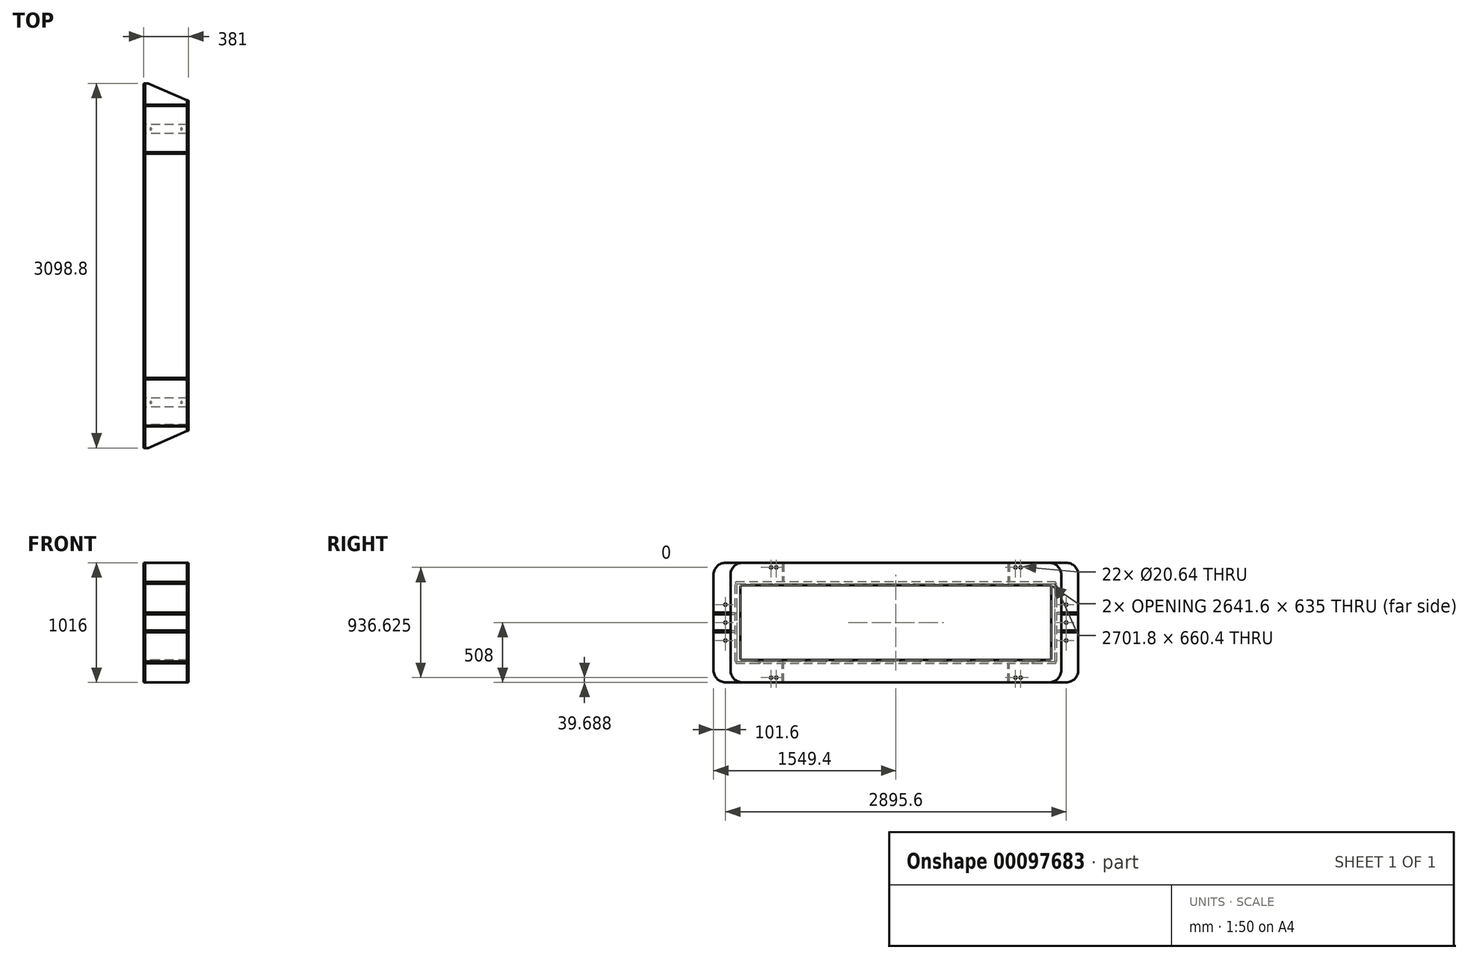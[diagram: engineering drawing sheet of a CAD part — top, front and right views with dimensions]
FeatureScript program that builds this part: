
annotation { "Feature Type Name" : "Feature", "Feature Type Description" : "" }
export const myFeature = defineFeature(function(context is Context, id is Id, definition is map)
    precondition{}
    {
        {
            var Q0;
            Q0=qCreatedBy(makeId("Right.planeOp"),FACE);
            var sketch = newSketch(context, id + "F0", { "sketchPlane" : qUnion([Q0])});
            skLineSegment(sketch, "E0.bottom", {"start": v(-1308.1, 317.5) * mm, "end": v(1308.1, 317.5) * mm});
            skLineSegment(sketch, "E0.top", {"start": v(-1308.1, -317.5) * mm, "end": v(1308.1, -317.5) * mm});
            skLineSegment(sketch, "E0.left", {"start": v(-1320.8, 304.8) * mm, "end": v(-1320.8, -304.8) * mm});
            skLineSegment(sketch, "E0.right", {"start": v(1320.8, 304.8) * mm, "end": v(1320.8, -304.8) * mm});
            skPoint(sketch, "E0.middle", {"position": v(0, 0) * mm});
            skLineSegment(sketch, "E1.bottom", {"start": v(-1447.8, 508) * mm, "end": v(1447.8, 508) * mm});
            skLineSegment(sketch, "E1.top", {"start": v(-1447.8, -508) * mm, "end": v(1447.8, -508) * mm});
            skLineSegment(sketch, "E1.left", {"start": v(-1549.4, 406.4) * mm, "end": v(-1549.4, -406.4) * mm});
            skLineSegment(sketch, "E1.right", {"start": v(1549.4, 406.4) * mm, "end": v(1549.4, -406.4) * mm});
            skLineSegment(sketch, "E2", {"start": v(-1633.4, 0) * mm, "end": v(1813.82, 0) * mm, "construction": true});
            skPoint(sketch, "E2.endSnap0", {"position": v(-1549.4, 0) * mm});
            skLineSegment(sketch, "E3", {"start": v(0, 873) * mm, "end": v(0, -1070.76) * mm, "construction": true});
            skLineSegment(sketch, "E4.0", {"start": v(-1447.8, 873) * mm, "end": v(-1447.8, -1070.76) * mm, "construction": true});
            skLineSegment(sketch, "E5.0", {"start": v(-1633.4, 152.4) * mm, "end": v(1813.82, 152.4) * mm, "construction": true});
            skLineSegment(sketch, "E6.0", {"start": v(-1633.4, -152.4) * mm, "end": v(1813.82, -152.4) * mm, "construction": true});
            skCircle(sketch, "E7", {"center": v(-1447.8, 152.4) * mm, "radius": 10.32 * mm});
            skCircle(sketch, "E8.0.1.0", {"center": v(-1447.8, 0) * mm, "radius": 10.32 * mm});
            skCircle(sketch, "E8.0.2.0", {"center": v(-1447.8, -152.4) * mm, "radius": 10.32 * mm});
            skLineSegment(sketch, "E8.direction1", {"start": v(-1447.8, 152.4) * mm, "end": v(-1422.4, 152.4) * mm, "construction": true});
            skLineSegment(sketch, "E8.direction2", {"start": v(-1447.8, 152.4) * mm, "end": v(-1447.8, 0) * mm, "construction": true});
            skLineSegment(sketch, "E9.MirrorCS", {"start": v(1447.8, 152.4) * mm, "end": v(1422.4, 152.4) * mm, "construction": true});
            skCircle(sketch, "E10.MirrorC", {"center": v(1447.8, 152.4) * mm, "radius": 10.32 * mm});
            skCircle(sketch, "E11.MirrorC", {"center": v(1447.8, 0) * mm, "radius": 10.32 * mm});
            skCircle(sketch, "E12.MirrorC", {"center": v(1447.8, -152.4) * mm, "radius": 10.32 * mm});
            skPoint(sketch, "E13.MirrorP", {"position": v(1549.4, 0) * mm});
            skLineSegment(sketch, "E14.MirrorCS", {"start": v(1447.8, 152.4) * mm, "end": v(1447.8, 0) * mm, "construction": true});
            skPoint(sketch, "E15.visualSharp", {"position": v(-1320.8, 317.5) * mm});
            skArc(sketch, "E15.filletArc", {"start": v(-1308.1, 317.5) * mm, "mid": v(-1317.08, 313.78) * mm, "end": v(-1320.8, 304.8) * mm});
            skPoint(sketch, "E16.visualSharp", {"position": v(-1320.8, -317.5) * mm});
            skArc(sketch, "E16.filletArc", {"start": v(-1320.8, -304.8) * mm, "mid": v(-1317.08, -313.78) * mm, "end": v(-1308.1, -317.5) * mm});
            skPoint(sketch, "E17.visualSharp", {"position": v(1320.8, -317.5) * mm});
            skArc(sketch, "E17.filletArc", {"start": v(1308.1, -317.5) * mm, "mid": v(1317.08, -313.78) * mm, "end": v(1320.8, -304.8) * mm});
            skPoint(sketch, "E18.visualSharp", {"position": v(1320.8, 317.5) * mm});
            skArc(sketch, "E18.filletArc", {"start": v(1320.8, 304.8) * mm, "mid": v(1317.08, 313.78) * mm, "end": v(1308.1, 317.5) * mm});
            skPoint(sketch, "E19.visualSharp", {"position": v(-1549.4, 508) * mm});
            skArc(sketch, "E19.filletArc", {"start": v(-1447.8, 508) * mm, "mid": v(-1519.64, 478.24) * mm, "end": v(-1549.4, 406.4) * mm});
            skPoint(sketch, "E20.visualSharp", {"position": v(-1549.4, -508) * mm});
            skArc(sketch, "E20.filletArc", {"start": v(-1549.4, -406.4) * mm, "mid": v(-1519.64, -478.24) * mm, "end": v(-1447.8, -508) * mm});
            skPoint(sketch, "E21.visualSharp", {"position": v(1549.4, 508) * mm});
            skArc(sketch, "E21.filletArc", {"start": v(1549.4, 406.4) * mm, "mid": v(1519.64, 478.24) * mm, "end": v(1447.8, 508) * mm});
            skPoint(sketch, "E22.visualSharp", {"position": v(1549.4, -508) * mm});
            skArc(sketch, "E22.filletArc", {"start": v(1447.8, -508) * mm, "mid": v(1519.64, -478.24) * mm, "end": v(1549.4, -406.4) * mm});
            skLineSegment(sketch, "E23.0", {"start": v(-1016, 873) * mm, "end": v(-1016, -1070.76) * mm, "construction": true});
            skLineSegment(sketch, "E24.0", {"start": v(-1633.4, 506.41) * mm, "end": v(1813.82, 506.41) * mm, "construction": true});
            skLineSegment(sketch, "E25.0", {"start": v(-1633.4, 468.31) * mm, "end": v(1813.82, 468.31) * mm, "construction": true});
            skLineSegment(sketch, "E26.0", {"start": v(-1060.45, 873) * mm, "end": v(-1060.45, -1070.76) * mm, "construction": true});
            skCircle(sketch, "E27", {"center": v(-1060.45, 468.31) * mm, "radius": 10.32 * mm});
            skCircle(sketch, "E28", {"center": v(-1016, 468.31) * mm, "radius": 10.32 * mm});
            skCircle(sketch, "E29.MirrorC", {"center": v(-1060.45, -468.31) * mm, "radius": 10.32 * mm});
            skCircle(sketch, "E30.MirrorC", {"center": v(-1016, -468.31) * mm, "radius": 10.32 * mm});
            skCircle(sketch, "E31.MirrorC", {"center": v(1060.45, 468.31) * mm, "radius": 10.32 * mm});
            skCircle(sketch, "E32.MirrorC", {"center": v(1016, 468.31) * mm, "radius": 10.32 * mm});
            skCircle(sketch, "E33.MirrorC", {"center": v(1016, -468.31) * mm, "radius": 10.32 * mm});
            skCircle(sketch, "E34.MirrorC", {"center": v(1060.45, -468.31) * mm, "radius": 10.32 * mm});
            skSolve(sketch);
        }
        {
            var Q0;
            Q0 = qSketchRegion(id + "F0", true);
            extrude(context, id + "F1", {"entities" : qUnion([Q0]), "depth" : 12.7 * mm});
        }
        {
            var Q0;
            Q0=makeQuery(id+"F1.opExtrude","CAP_FACE",FACE,{"disambiguationData":[OSD([sQuery(id+"F0.wireOp",EDGE,"E0.bottom"),sQuery(id+"F0.wireOp",EDGE,"E0.top"),sQuery(id+"F0.wireOp",EDGE,"E0.left"),sQuery(id+"F0.wireOp",EDGE,"E0.right"),sQuery(id+"F0.wireOp",EDGE,"E1.bottom"),sQuery(id+"F0.wireOp",EDGE,"E1.top"),sQuery(id+"F0.wireOp",EDGE,"E1.left"),sQuery(id+"F0.wireOp",EDGE,"E1.right"),sQuery(id+"F0.wireOp",EDGE,"E7"),sQuery(id+"F0.wireOp",EDGE,"E8.0.1.0"),sQuery(id+"F0.wireOp",EDGE,"E8.0.2.0"),sQuery(id+"F0.wireOp",EDGE,"E10.MirrorC"),sQuery(id+"F0.wireOp",EDGE,"E11.MirrorC"),sQuery(id+"F0.wireOp",EDGE,"E12.MirrorC"),sQuery(id+"F0.wireOp",EDGE,"E15.filletArc"),sQuery(id+"F0.wireOp",EDGE,"E16.filletArc"),sQuery(id+"F0.wireOp",EDGE,"E17.filletArc"),sQuery(id+"F0.wireOp",EDGE,"E18.filletArc"),sQuery(id+"F0.wireOp",EDGE,"E19.filletArc"),sQuery(id+"F0.wireOp",EDGE,"E20.filletArc"),sQuery(id+"F0.wireOp",EDGE,"E21.filletArc"),sQuery(id+"F0.wireOp",EDGE,"E22.filletArc"),sQuery(id+"F0.wireOp",EDGE,"E27"),sQuery(id+"F0.wireOp",EDGE,"E28"),sQuery(id+"F0.wireOp",EDGE,"E29.MirrorC"),sQuery(id+"F0.wireOp",EDGE,"E30.MirrorC"),sQuery(id+"F0.wireOp",EDGE,"E31.MirrorC"),sQuery(id+"F0.wireOp",EDGE,"E32.MirrorC"),sQuery(id+"F0.wireOp",EDGE,"E33.MirrorC"),sQuery(id+"F0.wireOp",EDGE,"E34.MirrorC")])],"isStart":false});
            var sketch = newSketch(context, id + "F2", { "sketchPlane" : qUnion([Q0])});
            skLineSegment(sketch, "E35.0", {"start": v(-1308.1, -317.5) * mm, "end": v(1308.1, -317.5) * mm, "construction": true});
            skLineSegment(sketch, "E36", {"start": v(-1689.68, 0) * mm, "end": v(1686.9, 0) * mm, "construction": true});
            skLineSegment(sketch, "E37", {"start": v(0, 776.11) * mm, "end": v(0, -698.36) * mm, "construction": true});
            skLineSegment(sketch, "E38.0", {"start": v(-1689.68, -317.5) * mm, "end": v(1686.9, -317.5) * mm, "construction": true});
            skLineSegment(sketch, "E39.0", {"start": v(-1162.05, 776.11) * mm, "end": v(-1162.05, -698.36) * mm, "construction": true});
            skLineSegment(sketch, "E40.0", {"start": v(-1200.15, 776.11) * mm, "end": v(-1200.15, -698.36) * mm, "construction": true});
            skLineSegment(sketch, "E41.bottom", {"start": v(-1200.15, -317.5) * mm, "end": v(-1123.95, -317.5) * mm});
            skLineSegment(sketch, "E41.top", {"start": v(-1200.15, -330.2) * mm, "end": v(-1123.95, -330.2) * mm});
            skLineSegment(sketch, "E41.left", {"start": v(-1200.15, -317.5) * mm, "end": v(-1200.15, -330.2) * mm});
            skLineSegment(sketch, "E41.right", {"start": v(-1123.95, -317.5) * mm, "end": v(-1123.95, -330.2) * mm});
            skLineSegment(sketch, "E42.bottom", {"start": v(-1358.9, -330.2) * mm, "end": v(0, -330.2) * mm});
            skLineSegment(sketch, "E42.top", {"start": v(-1358.9, -345.95) * mm, "end": v(0, -345.95) * mm});
            skLineSegment(sketch, "E42.left", {"start": v(-1358.9, -330.2) * mm, "end": v(-1358.9, -345.95) * mm});
            skLineSegment(sketch, "E42.right", {"start": v(0, -330.2) * mm, "end": v(0, -345.95) * mm});
            skLineSegment(sketch, "E43.MirrorCS", {"start": v(1200.15, -317.5) * mm, "end": v(1200.15, -330.2) * mm});
            skLineSegment(sketch, "E44.MirrorCS", {"start": v(1123.95, -317.5) * mm, "end": v(1123.95, -330.2) * mm});
            skLineSegment(sketch, "E45.MirrorCS", {"start": v(1358.9, -330.2) * mm, "end": v(1358.9, -345.95) * mm});
            skLineSegment(sketch, "E46.MirrorCS", {"start": v(1200.15, -330.2) * mm, "end": v(1123.95, -330.2) * mm});
            skLineSegment(sketch, "E47.MirrorCS", {"start": v(1200.15, -317.5) * mm, "end": v(1123.95, -317.5) * mm});
            skLineSegment(sketch, "E48.MirrorCS", {"start": v(1358.9, -330.2) * mm, "end": v(0, -330.2) * mm});
            skLineSegment(sketch, "E49.MirrorCS", {"start": v(1358.9, -345.95) * mm, "end": v(0, -345.95) * mm});
            skLineSegment(sketch, "E50.bottom", {"start": v(-1366.9, -330.2) * mm, "end": v(-1350.9, -330.2) * mm});
            skLineSegment(sketch, "E50.top", {"start": v(-1366.9, 0) * mm, "end": v(-1350.9, 0) * mm});
            skLineSegment(sketch, "E50.left", {"start": v(-1366.9, -330.2) * mm, "end": v(-1366.9, 0) * mm});
            skLineSegment(sketch, "E50.right", {"start": v(-1350.9, -330.2) * mm, "end": v(-1350.9, 0) * mm});
            skLineSegment(sketch, "E51.bottom", {"start": v(-1358.9, -330.2) * mm, "end": v(-1358.9, -330.2) * mm});
            skLineSegment(sketch, "E51.top", {"start": v(-1358.9, -330.2) * mm, "end": v(-1358.9, -330.2) * mm});
            skLineSegment(sketch, "E51.left", {"start": v(-1358.9, -330.2) * mm, "end": v(-1358.9, -330.2) * mm});
            skLineSegment(sketch, "E51.right", {"start": v(-1358.9, -330.2) * mm, "end": v(-1358.9, -330.2) * mm});
            skLineSegment(sketch, "E52.MirrorCS", {"start": v(-1366.9, 330.2) * mm, "end": v(-1350.9, 330.2) * mm});
            skLineSegment(sketch, "E53.MirrorCS", {"start": v(-1358.9, 330.2) * mm, "end": v(-1358.9, 330.2) * mm});
            skLineSegment(sketch, "E54.MirrorCS", {"start": v(-1358.9, 330.2) * mm, "end": v(-1358.9, 345.95) * mm});
            skLineSegment(sketch, "E55.MirrorCS", {"start": v(-1350.9, 330.2) * mm, "end": v(-1350.9, 0) * mm});
            skLineSegment(sketch, "E56.MirrorCS", {"start": v(-1366.9, 330.2) * mm, "end": v(-1366.9, 0) * mm});
            skLineSegment(sketch, "E57.MirrorCS", {"start": v(1366.9, 0) * mm, "end": v(1350.9, 0) * mm});
            skLineSegment(sketch, "E58.MirrorCS", {"start": v(1366.9, 330.2) * mm, "end": v(1350.9, 330.2) * mm});
            skLineSegment(sketch, "E59.MirrorCS", {"start": v(1366.9, -330.2) * mm, "end": v(1350.9, -330.2) * mm});
            skLineSegment(sketch, "E60.MirrorCS", {"start": v(1358.9, -330.2) * mm, "end": v(1358.9, -330.2) * mm});
            skLineSegment(sketch, "E61.MirrorCS", {"start": v(1358.9, 330.2) * mm, "end": v(1358.9, 330.2) * mm});
            skLineSegment(sketch, "E62.MirrorCS", {"start": v(1358.9, 330.2) * mm, "end": v(1358.9, 345.95) * mm});
            skLineSegment(sketch, "E63.MirrorCS", {"start": v(1350.9, 330.2) * mm, "end": v(1350.9, 0) * mm});
            skLineSegment(sketch, "E64.MirrorCS", {"start": v(1366.9, 330.2) * mm, "end": v(1366.9, 0) * mm});
            skLineSegment(sketch, "E65.MirrorCS", {"start": v(1366.9, -330.2) * mm, "end": v(1366.9, 0) * mm});
            skLineSegment(sketch, "E66.MirrorCS", {"start": v(1350.9, -330.2) * mm, "end": v(1350.9, 0) * mm});
            skLineSegment(sketch, "E67.MirrorCS", {"start": v(-1358.9, 330.2) * mm, "end": v(0, 330.2) * mm});
            skLineSegment(sketch, "E68.MirrorCS", {"start": v(-1358.9, 345.95) * mm, "end": v(0, 345.95) * mm});
            skLineSegment(sketch, "E69.MirrorCS", {"start": v(1358.9, 330.2) * mm, "end": v(0, 330.2) * mm});
            skLineSegment(sketch, "E70.MirrorCS", {"start": v(1358.9, 345.95) * mm, "end": v(0, 345.95) * mm});
            skSolve(sketch);
        }
        {
            var Q0;
            Q0 = qSketchRegion(id + "F2", true);
            extrude(context, id + "F3", {"entities" : qUnion([Q0]), "depth" : 355.6 * mm});
        }
        {
            var Q0;
            Q0=makeQuery(id+"F2.imprint","IMPRINT",FACE,{"disambiguationData":[TD([[makeQuery(id+"F2.imprint","IMPRINT",EDGE,{"derivedFrom":sQuery(id+"F2.wireOp",EDGE,"E41.bottom")}),-1.0]])]});
            var Q1;
            {var subQ0=sQuery(id+"F2.wireOp",EDGE,"E43.MirrorCS");Q1=makeQuery(id+"F2.imprint","IMPRINT",FACE,{"disambiguationData":[TD([[makeQuery(id+"F2.imprint","IMPRINT",EDGE,{"derivedFrom":subQ0}),-1.0]])]});}
            extrude(context, id + "F4", {"entities" : qUnion([Q0, Q1]), "depth" : 355.6 * mm});
        }
        {
            var Q0;
            Q0=makeQuery(id+"F3.opExtrude","SWEPT_FACE",FACE,{"disambiguationData":[OSD([sQuery(id+"F2.wireOp",EDGE,"E42.top"),sQuery(id+"F2.wireOp",EDGE,"E49.MirrorCS")])]});
            var sketch = newSketch(context, id + "F5", { "sketchPlane" : qUnion([Q0])});
            skLineSegment(sketch, "E71", {"start": v(190.5, 1358.9) * mm, "end": v(190.5, -1433.66) * mm, "construction": true});
            skLineSegment(sketch, "E72", {"start": v(595.8, 0) * mm, "end": v(-191.18, 0) * mm, "construction": true});
            skLineSegment(sketch, "E73.0", {"start": v(595.8, 1162.05) * mm, "end": v(-191.18, 1162.05) * mm, "construction": true});
            skLineSegment(sketch, "E74.0", {"start": v(320.68, 1358.9) * mm, "end": v(320.68, -1433.66) * mm, "construction": true});
            skCircle(sketch, "E75", {"center": v(320.68, 1162.05) * mm, "radius": 8 * mm});
            skCircle(sketch, "E76.MirrorC", {"center": v(60.32, 1162.05) * mm, "radius": 8 * mm});
            skCircle(sketch, "E77.MirrorC", {"center": v(60.32, -1162.05) * mm, "radius": 8 * mm});
            skCircle(sketch, "E78.MirrorC", {"center": v(320.68, -1162.05) * mm, "radius": 8 * mm});
            skSolve(sketch);
        }
        {
            var Q0;
            Q0 = qSketchRegion(id + "F5", true);
            extrude(context, id + "F6", {"entities" : qUnion([Q0]), "operationType" : NewBodyOperationType.REMOVE, "oppositeDirection" : true, "depth" : 152.4 * mm});
        }
        {
            var Q0;
            Q0=makeQuery(id+"F2.imprint","IMPRINT",FACE,{"disambiguationData":[TD([[makeQuery(id+"F2.imprint","IMPRINT",EDGE,{"derivedFrom":sQuery(id+"F2.wireOp",EDGE,"E42.top")}),-1.0]])]});
            var sketch = newSketch(context, id + "F7", { "sketchPlane" : qUnion([Q0])});
            skCircle(sketch, "E79.0", {"center": v(-1447.8, 152.4) * mm, "radius": 10.32 * mm, "construction": true});
            skCircle(sketch, "E80.0", {"center": v(-1447.8, 0) * mm, "radius": 10.32 * mm, "construction": true});
            skLineSegment(sketch, "E81.0", {"start": v(-1549.4, 406.4) * mm, "end": v(-1549.4, -406.4) * mm, "construction": true});
            skLineSegment(sketch, "E82.0", {"start": v(-1366.9, 330.2) * mm, "end": v(-1366.9, 0) * mm, "construction": true});
            skLineSegment(sketch, "E83", {"start": v(-1447.8, 152.4) * mm, "end": v(-1447.8, 0) * mm, "construction": true});
            skLineSegment(sketch, "E84", {"start": v(-1447.8, 76.2) * mm, "end": v(-1629.34, 76.2) * mm, "construction": true});
            skLineSegment(sketch, "E85.bottom", {"start": v(-1549.4, 84.2) * mm, "end": v(-1366.9, 84.2) * mm});
            skLineSegment(sketch, "E85.top", {"start": v(-1549.4, 68.2) * mm, "end": v(-1366.9, 68.2) * mm});
            skLineSegment(sketch, "E85.left", {"start": v(-1549.4, 84.2) * mm, "end": v(-1549.4, 68.2) * mm});
            skLineSegment(sketch, "E85.right", {"start": v(-1366.9, 84.2) * mm, "end": v(-1366.9, 68.2) * mm});
            skSolve(sketch);
        }
        {
            var Q0;
            Q0 = qSketchRegion(id + "F7", true);
            extrude(context, id + "F8", {"entities" : qUnion([Q0]), "depth" : 355.6 * mm});
        }
        {
            var Q0;
            Q0=makeQuery(id+"F3.opExtrude","CAP_FACE",FACE,{"disambiguationData":[OSD([sQuery(id+"F2.wireOp",EDGE,"E42.bottom"),sQuery(id+"F2.wireOp",EDGE,"E42.top"),sQuery(id+"F2.wireOp",EDGE,"E42.left"),sQuery(id+"F2.wireOp",EDGE,"E48.MirrorCS"),sQuery(id+"F2.wireOp",EDGE,"E49.MirrorCS"),sQuery(id+"F2.wireOp",EDGE,"E50.bottom"),sQuery(id+"F2.wireOp",EDGE,"E50.left"),sQuery(id+"F2.wireOp",EDGE,"E50.right"),sQuery(id+"F2.wireOp",EDGE,"E52.MirrorCS"),sQuery(id+"F2.wireOp",EDGE,"E54.MirrorCS"),sQuery(id+"F2.wireOp",EDGE,"E55.MirrorCS"),sQuery(id+"F2.wireOp",EDGE,"E56.MirrorCS"),sQuery(id+"F2.wireOp",EDGE,"E58.MirrorCS"),sQuery(id+"F2.wireOp",EDGE,"E59.MirrorCS"),sQuery(id+"F2.wireOp",EDGE,"E45.MirrorCS"),sQuery(id+"F2.wireOp",EDGE,"E62.MirrorCS"),sQuery(id+"F2.wireOp",EDGE,"E63.MirrorCS"),sQuery(id+"F2.wireOp",EDGE,"E64.MirrorCS"),sQuery(id+"F2.wireOp",EDGE,"E65.MirrorCS"),sQuery(id+"F2.wireOp",EDGE,"E66.MirrorCS"),sQuery(id+"F2.wireOp",EDGE,"E67.MirrorCS"),sQuery(id+"F2.wireOp",EDGE,"E68.MirrorCS"),sQuery(id+"F2.wireOp",EDGE,"E69.MirrorCS"),sQuery(id+"F2.wireOp",EDGE,"E70.MirrorCS")])],"isStart":false});
            var sketch = newSketch(context, id + "F9", { "sketchPlane" : qUnion([Q0])});
            skLineSegment(sketch, "E86.0", {"start": v(-1308.1, 317.5) * mm, "end": v(1308.1, 317.5) * mm});
            skLineSegment(sketch, "E87.0.0", {"start": v(1447.8, 508) * mm, "end": v(-1303.4, 508) * mm});
            skLineSegment(sketch, "E87.0.4", {"start": v(-1303.4, -508) * mm, "end": v(1447.8, -508) * mm});
            skLineSegment(sketch, "E88.0", {"start": v(-1320.8, 304.8) * mm, "end": v(-1320.8, -304.8) * mm});
            skArc(sketch, "E89.0", {"start": v(-1320.8, -304.8) * mm, "mid": v(-1317.08, -313.78) * mm, "end": v(-1308.1, -317.5) * mm});
            skLineSegment(sketch, "E90.0.0", {"start": v(1308.1, 317.5) * mm, "end": v(-1308.1, 317.5) * mm});
            skArc(sketch, "E90.0.1", {"start": v(-1308.1, 317.5) * mm, "mid": v(-1317.08, 313.78) * mm, "end": v(-1320.8, 304.8) * mm});
            skLineSegment(sketch, "E90.0.4", {"start": v(-1308.1, -317.5) * mm, "end": v(-1200.15, -317.5) * mm});
            skLineSegment(sketch, "E90.0.5", {"start": v(-1200.15, -317.5) * mm, "end": v(-1123.95, -317.5) * mm});
            skLineSegment(sketch, "E90.0.6", {"start": v(-1123.95, -317.5) * mm, "end": v(1123.95, -317.5) * mm});
            skLineSegment(sketch, "E90.0.7", {"start": v(1123.95, -317.5) * mm, "end": v(1200.15, -317.5) * mm});
            skLineSegment(sketch, "E90.0.8", {"start": v(1200.15, -317.5) * mm, "end": v(1308.1, -317.5) * mm});
            skArc(sketch, "E90.0.9", {"start": v(1308.1, -317.5) * mm, "mid": v(1317.08, -313.78) * mm, "end": v(1320.8, -304.8) * mm});
            skLineSegment(sketch, "E90.0.10", {"start": v(1320.8, -304.8) * mm, "end": v(1320.8, 304.8) * mm});
            skArc(sketch, "E90.0.11", {"start": v(1320.8, 304.8) * mm, "mid": v(1317.08, 313.78) * mm, "end": v(1308.1, 317.5) * mm});
            skLineSegment(sketch, "E91.trimOffspring", {"start": v(-1308.1, -317.5) * mm, "end": v(1308.1, -317.5) * mm});
            skPoint(sketch, "E92.0.start.orphan", {"position": v(-1689.68, -317.5) * mm});
            skPoint(sketch, "E93.orphan", {"position": v(1686.9, -317.5) * mm});
            skPoint(sketch, "E87.0.2.end.orphan", {"position": v(-1549.4, -406.4) * mm});
            skPoint(sketch, "E87.0.1.end.orphan", {"position": v(-1549.4, 406.4) * mm});
            skPoint(sketch, "E87.0.6.end.orphan", {"position": v(1549.4, 406.4) * mm});
            skPoint(sketch, "E87.0.5.end.orphan", {"position": v(1549.4, -406.4) * mm});
            skLineSegment(sketch, "E94.0", {"start": v(-1366.9, -330.2) * mm, "end": v(-1366.9, 330.2) * mm, "construction": true});
            skLineSegment(sketch, "E95.0", {"start": v(-1405, -406.4) * mm, "end": v(-1405, 406.4) * mm});
            skPoint(sketch, "E96.newPointB", {"position": v(-1447.8, -508) * mm});
            skArc(sketch, "E96.filletArc", {"start": v(-1405, -406.4) * mm, "mid": v(-1375.24, -478.24) * mm, "end": v(-1303.4, -508) * mm});
            skPoint(sketch, "E97.newPointB", {"position": v(-1447.8, 508) * mm});
            skArc(sketch, "E97.filletArc", {"start": v(-1303.4, 508) * mm, "mid": v(-1375.24, 478.24) * mm, "end": v(-1405, 406.4) * mm});
            skArc(sketch, "E98.MirrorCS", {"start": v(1303.4, 508) * mm, "mid": v(1375.24, 478.24) * mm, "end": v(1405, 406.4) * mm});
            skLineSegment(sketch, "E99.MirrorCS", {"start": v(1405, -406.4) * mm, "end": v(1405, 406.4) * mm});
            skArc(sketch, "E100.MirrorCS", {"start": v(1405, -406.4) * mm, "mid": v(1375.24, -478.24) * mm, "end": v(1303.4, -508) * mm});
            skCircle(sketch, "E101.0", {"center": v(-1060.45, 468.31) * mm, "radius": 10.32 * mm});
            skCircle(sketch, "E102.0", {"center": v(-1016, 468.31) * mm, "radius": 10.32 * mm});
            skCircle(sketch, "E103.0", {"center": v(1016, 468.31) * mm, "radius": 10.32 * mm});
            skCircle(sketch, "E104.0", {"center": v(1060.45, 468.31) * mm, "radius": 10.32 * mm});
            skCircle(sketch, "E105.0", {"center": v(-1060.45, -468.31) * mm, "radius": 10.32 * mm});
            skCircle(sketch, "E106.0", {"center": v(-1016, -468.31) * mm, "radius": 10.32 * mm});
            skCircle(sketch, "E107.0", {"center": v(1016, -468.31) * mm, "radius": 10.32 * mm});
            skCircle(sketch, "E108.0", {"center": v(1060.45, -468.31) * mm, "radius": 10.32 * mm});
            skSolve(sketch);
        }
        {
            var Q0;
            Q0 = qSketchRegion(id + "F9", true);
            extrude(context, id + "F10", {"entities" : qUnion([Q0]), "depth" : 12.7 * mm});
        }
        {
            var Q0;
            Q0=makeQuery(id+"F8.opExtrude","SWEPT_FACE",FACE,{"disambiguationData":[OSD([sQuery(id+"F7.wireOp",EDGE,"E85.bottom")])]});
            var sketch = newSketch(context, id + "F11", { "sketchPlane" : qUnion([Q0])});
            skLineSegment(sketch, "E109.0", {"start": v(38.1, -1689.68) * mm, "end": v(38.1, 1686.9) * mm, "construction": true});
            skLineSegment(sketch, "E110.0", {"start": v(381, -1405) * mm, "end": v(368.3, -1405) * mm, "construction": true});
            skLineSegment(sketch, "E111.0", {"start": v(368.3, -1549.4) * mm, "end": v(368.3, -1366.9) * mm});
            skLineSegment(sketch, "E112.0", {"start": v(368.3, -1549.4) * mm, "end": v(12.7, -1549.4) * mm});
            skLineSegment(sketch, "E113", {"start": v(38.1, -1549.4) * mm, "end": v(368.3, -1405) * mm});
            skSolve(sketch);
        }
        {
            var Q0;
            Q0 = qSketchRegion(id + "F11", true);
            extrude(context, id + "F12", {"entities" : qUnion([Q0]), "operationType" : NewBodyOperationType.REMOVE, "endBound" : BoundingType.THROUGH_ALL, "oppositeDirection" : true, "depth" : 25.4 * mm});
        }
        {
            var Q0;
            Q0=makeQuery(id+"F8.opExtrude","SWEPT_BODY",BODY,{"disambiguationData":[OSD([sQuery(id+"F7.wireOp",EDGE,"E85.bottom"),sQuery(id+"F7.wireOp",EDGE,"E85.top"),sQuery(id+"F7.wireOp",EDGE,"E85.left"),sQuery(id+"F7.wireOp",EDGE,"E85.right")])]});
            var Q1;
            Q1=qCreatedBy(makeId("Top.planeOp"),FACE);
            mirror(context, id + "F13", {"entities" : qUnion([Q0]), "mirrorPlane" : qUnion([Q1])});
        }
        {
            var Q0;
            Q0=makeQuery(id+"F8.opExtrude","SWEPT_BODY",BODY,{"disambiguationData":[OSD([sQuery(id+"F7.wireOp",EDGE,"E85.bottom"),sQuery(id+"F7.wireOp",EDGE,"E85.top"),sQuery(id+"F7.wireOp",EDGE,"E85.left"),sQuery(id+"F7.wireOp",EDGE,"E85.right")])]});
            var Q1;
            Q1=makeQuery(id+"F13.opPattern","COPY",BODY,{"derivedFrom":makeQuery(id+"F8.opExtrude","SWEPT_BODY",BODY,{"disambiguationData":[OSD([sQuery(id+"F7.wireOp",EDGE,"E85.bottom"),sQuery(id+"F7.wireOp",EDGE,"E85.top"),sQuery(id+"F7.wireOp",EDGE,"E85.left"),sQuery(id+"F7.wireOp",EDGE,"E85.right")])]}),"instanceName":"1"});
            var Q2;
            Q2=qCreatedBy(makeId("Front.planeOp"),FACE);
            mirror(context, id + "F14", {"entities" : qUnion([Q0, Q1]), "mirrorPlane" : qUnion([Q2])});
        }
        {
            var Q0;
            Q0=makeQuery(id+"F4.opExtrude","SWEPT_FACE",FACE,{"disambiguationData":[OSD([sQuery(id+"F2.wireOp",EDGE,"E47.MirrorCS")])]});
            var sketch = newSketch(context, id + "F15", { "sketchPlane" : qUnion([Q0])});
            skCircle(sketch, "E114.0", {"center": v(320.68, 1162.05) * mm, "radius": 8 * mm});
            skCircle(sketch, "E115.0", {"center": v(60.32, 1162.05) * mm, "radius": 8 * mm});
            skSolve(sketch);
        }
        {
            var Q0;
            Q0 = qSketchRegion(id + "F15", true);
            extrude(context, id + "F16", {"entities" : qUnion([Q0]), "operationType" : NewBodyOperationType.REMOVE, "oppositeDirection" : true, "depth" : 25.4 * mm});
        }
        {
            var Q0;
            Q0=makeQuery(id+"F4.opExtrude","SWEPT_FACE",FACE,{"disambiguationData":[OSD([sQuery(id+"F2.wireOp",EDGE,"E41.bottom")])]});
            var sketch = newSketch(context, id + "F17", { "sketchPlane" : qUnion([Q0])});
            skCircle(sketch, "E116.0", {"center": v(320.68, -1162.05) * mm, "radius": 8 * mm});
            skCircle(sketch, "E117.0", {"center": v(60.32, -1162.05) * mm, "radius": 8 * mm});
            skSolve(sketch);
        }
        {
            var Q0;
            Q0 = qSketchRegion(id + "F17", true);
            extrude(context, id + "F18", {"entities" : qUnion([Q0]), "operationType" : NewBodyOperationType.REMOVE, "oppositeDirection" : true, "depth" : 25.4 * mm});
        }
        {
            var Q0;
            Q0=makeQuery(id+"F3.opExtrude","SWEPT_FACE",FACE,{"disambiguationData":[OSD([sQuery(id+"F2.wireOp",EDGE,"E68.MirrorCS"),sQuery(id+"F2.wireOp",EDGE,"E70.MirrorCS")])]});
            var sketch = newSketch(context, id + "F19", { "sketchPlane" : qUnion([Q0])});
            skLineSegment(sketch, "E118", {"start": v(-343.73, 0) * mm, "end": v(504.34, 0) * mm, "construction": true});
            skLineSegment(sketch, "E119.0", {"start": v(12.7, -965.2) * mm, "end": v(368.3, -965.2) * mm});
            skLineSegment(sketch, "E120.0", {"start": v(12.7, -952.5) * mm, "end": v(368.3, -952.5) * mm});
            skLineSegment(sketch, "E121.0", {"start": v(12.7, -1358.9) * mm, "end": v(12.7, 0) * mm});
            skLineSegment(sketch, "E122.0", {"start": v(368.3, 1303.4) * mm, "end": v(368.3, -1303.4) * mm});
            skSolve(sketch);
        }
        {
            var Q0;
            Q0 = qSketchRegion(id + "F19", true);
            var Q1;
            Q1=makeQuery(id+"F1.opExtrude","SWEPT_FACE",FACE,{"disambiguationData":[OSD([sQuery(id+"F0.wireOp",EDGE,"E1.bottom")])]});
            extrude(context, id + "F20", {"entities" : qUnion([Q0]), "endBound" : BoundingType.UP_TO_SURFACE, "endBoundEntityFace" : qUnion([Q1]), "depth" : 25.4 * mm});
        }
        {
            var Q0;
            Q0=makeQuery(id+"F20.opExtrude","SWEPT_BODY",BODY,{"disambiguationData":[OSD([sQuery(id+"F19.wireOp",EDGE,"E119.0"),sQuery(id+"F19.wireOp",EDGE,"E120.0"),sQuery(id+"F19.wireOp",EDGE,"E121.0"),sQuery(id+"F19.wireOp",EDGE,"E122.0")])]});
            var Q1;
            Q1=qCreatedBy(makeId("Front.planeOp"),FACE);
            mirror(context, id + "F21", {"entities" : qUnion([Q0]), "mirrorPlane" : qUnion([Q1])});
        }
        {
            var Q0;
            Q0=makeQuery(id+"F20.opExtrude","SWEPT_BODY",BODY,{"disambiguationData":[OSD([sQuery(id+"F19.wireOp",EDGE,"E119.0"),sQuery(id+"F19.wireOp",EDGE,"E120.0"),sQuery(id+"F19.wireOp",EDGE,"E121.0"),sQuery(id+"F19.wireOp",EDGE,"E122.0")])]});
            var Q1;
            Q1=makeQuery(id+"F21.opPattern","COPY",BODY,{"derivedFrom":makeQuery(id+"F20.opExtrude","SWEPT_BODY",BODY,{"disambiguationData":[OSD([sQuery(id+"F19.wireOp",EDGE,"E119.0"),sQuery(id+"F19.wireOp",EDGE,"E120.0"),sQuery(id+"F19.wireOp",EDGE,"E121.0"),sQuery(id+"F19.wireOp",EDGE,"E122.0")])]}),"instanceName":"1"});
            var Q2;
            Q2=qCreatedBy(makeId("Top.planeOp"),FACE);
            mirror(context, id + "F22", {"entities" : qUnion([Q0, Q1]), "mirrorPlane" : qUnion([Q2])});
        }
    });
